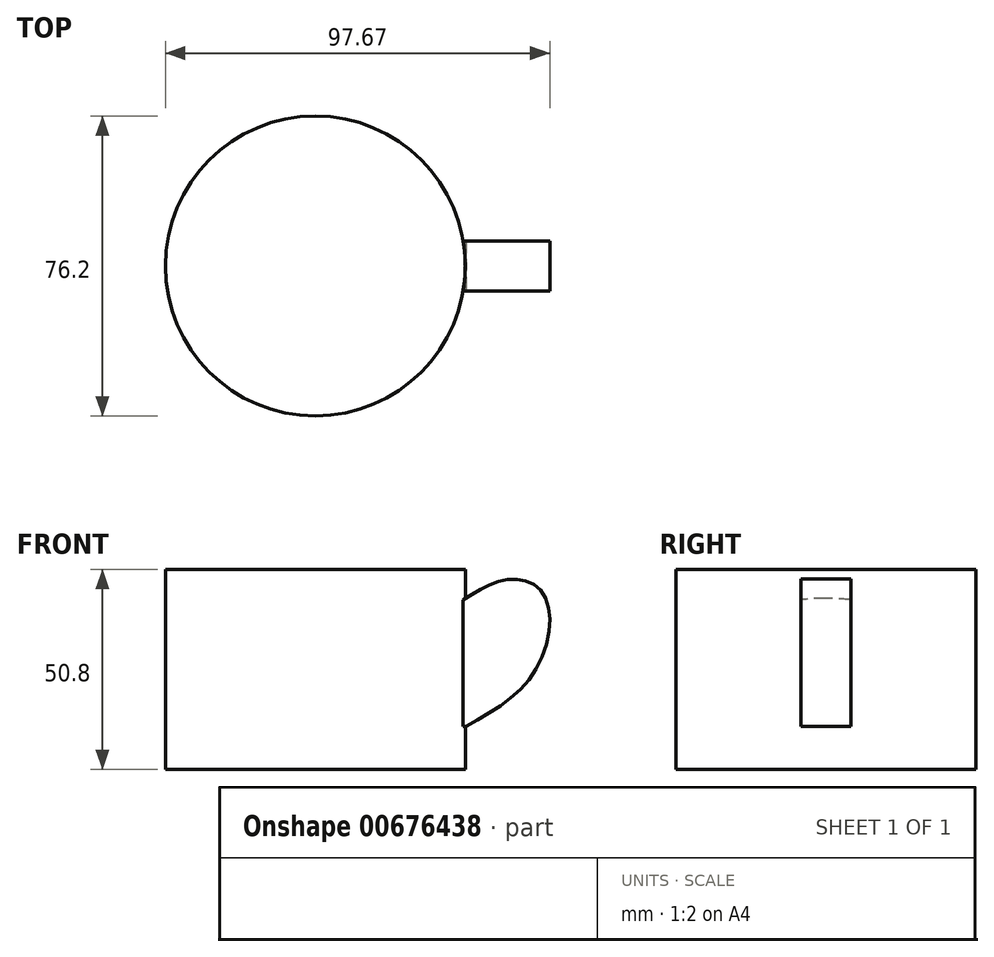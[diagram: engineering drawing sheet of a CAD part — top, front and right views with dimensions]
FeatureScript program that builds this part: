
annotation { "Feature Type Name" : "Feature", "Feature Type Description" : "" }
export const myFeature = defineFeature(function(context is Context, id is Id, definition is map)
    precondition{}
    {
        {
            var Q0;
            Q0=qCreatedBy(makeId("Top.planeOp"),FACE);
            var sketch = newSketch(context, id + "F0", { "sketchPlane" : qUnion([Q0])});
            skCircle(sketch, "E0", {"center": v(0, 0) * mm, "radius": 38.1 * mm});
            skSolve(sketch);
        }
        {
            var Q0;
            Q0=makeQuery(id+"F0.imprint","IMPRINT",FACE,{"disambiguationData":[TD([[makeQuery(id+"F0.imprint","IMPRINT",EDGE,{"derivedFrom":sQuery(id+"F0.wireOp",EDGE,"E0")}),1.0]])]});
            extrude(context, id + "F1", {"entities" : qUnion([Q0]), "depth" : 25.4 * mm, "offsetDistance" : 25.4 * mm});
        }
        {
            var Q0;
            Q0=qCreatedBy(makeId("Top.planeOp"),FACE);
            var sketch = newSketch(context, id + "F2", { "sketchPlane" : qUnion([Q0])});
            skCircle(sketch, "E1", {"center": v(0, 0) * mm, "radius": 38.1 * mm});
            skSolve(sketch);
        }
        {
            var Q0;
            Q0=makeQuery(id+"F2.imprint","IMPRINT",FACE,{"disambiguationData":[TD([[makeQuery(id+"F2.imprint","IMPRINT",EDGE,{"derivedFrom":sQuery(id+"F2.wireOp",EDGE,"E1")}),1.0]])]});
            extrude(context, id + "F3", {"entities" : qUnion([Q0]), "operationType" : NewBodyOperationType.ADD, "depth" : 25.4 * mm, "offsetDistance" : 25.4 * mm});
        }
        {
            var Q0;
            Q0=makeQuery(id+"F1.opExtrude","CAP_FACE",FACE,{"disambiguationData":[OSD([sQuery(id+"F0.wireOp",EDGE,"E0")])],"isStart":true});
            extrude(context, id + "F4", {"entities" : qUnion([Q0]), "operationType" : NewBodyOperationType.ADD, "depth" : 25.4 * mm, "offsetDistance" : 25.4 * mm});
        }
        {
            var Q0;
            Q0=qCreatedBy(makeId("Front.planeOp"),FACE);
            var sketch = newSketch(context, id + "F5", { "sketchPlane" : qUnion([Q0])});
            skFitSpline(sketch, "E2", {"points": [v(37.36, 17.59) * mm, v(49.19, 22.88) * mm, v(58.22, 18.84) * mm, v(56.04, 0) * mm, v(38.3, -14.48) * mm], "startDerivative": vector(51.44, 32.31) * mm, "endDerivative": vector(-68.8, -38.94) * mm});
            skLineSegment(sketch, "E3", {"start": v(37.36, 17.59) * mm, "end": v(37.36, -14.43) * mm});
            skLineSegment(sketch, "E4", {"start": v(37.36, -14.43) * mm, "end": v(38.3, -14.48) * mm});
            skFitSpline(sketch, "E5", {"points": [v(40.44, 13.58) * mm, v(44.62, 15.94) * mm, v(48.03, 16.99) * mm, v(52.35, 15.8) * mm, v(53.53, 13.19) * mm, v(53.92, 11.62) * mm, v(54.18, 8.22) * mm, v(53.13, 4.42) * mm, v(50.51, 1.93) * mm, v(47.9, 0) * mm, v(47.9, 0) * mm, v(46.98, -0.95) * mm, v(45.67, -1.73) * mm, v(45.02, -2.26) * mm, v(43.84, -2.91) * mm, v(43.32, -3.3) * mm, v(42.92, -3.3) * mm, v(41.61, 3.11) * mm, v(41.35, 6.12) * mm, v(40.44, 13.58) * mm]});
            skSolve(sketch);
        }
        {
            var Q0;
            Q0=makeQuery(id+"F5.imprint","IMPRINT",FACE,{"disambiguationData":[TD([[makeQuery(id+"F5.imprint","IMPRINT",EDGE,{"derivedFrom":sQuery(id+"F5.wireOp",EDGE,"E2")}),-1.0]])]});
            extrude(context, id + "F6", {"entities" : qUnion([Q0]), "operationType" : NewBodyOperationType.ADD, "endBound" : BoundingType.SYMMETRIC, "oppositeDirection" : true, "depth" : 12.7 * mm, "offsetDistance" : 25.4 * mm});
        }
    });
